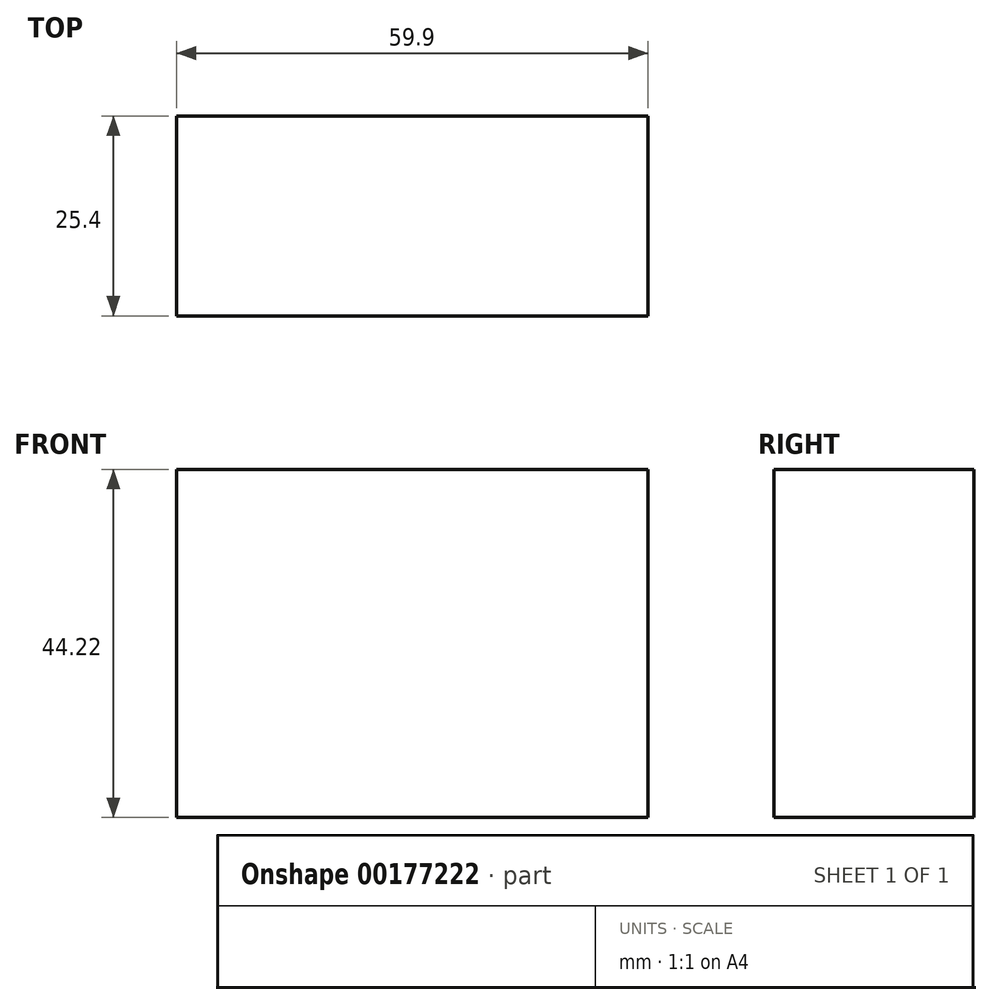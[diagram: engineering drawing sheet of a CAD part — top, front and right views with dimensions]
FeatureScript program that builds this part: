
annotation { "Feature Type Name" : "Feature", "Feature Type Description" : "" }
export const myFeature = defineFeature(function(context is Context, id is Id, definition is map)
    precondition{}
    {
        {
            var Q0;
            Q0=qCreatedBy(makeId("Front.planeOp"),FACE);
            var sketch = newSketch(context, id + "F0", { "sketchPlane" : qUnion([Q0])});
            skLineSegment(sketch, "E0.bottom", {"start": v(-42.5, 40.08) * mm, "end": v(17.4, 40.08) * mm});
            skLineSegment(sketch, "E0.top", {"start": v(-42.5, -4.14) * mm, "end": v(17.4, -4.14) * mm});
            skLineSegment(sketch, "E0.left", {"start": v(-42.5, 40.08) * mm, "end": v(-42.5, -4.14) * mm});
            skLineSegment(sketch, "E0.right", {"start": v(17.4, 40.08) * mm, "end": v(17.4, -4.14) * mm});
            skSolve(sketch);
        }
        {
            var Q0;
            Q0=makeQuery(id+"F0.imprint","IMPRINT",FACE,{"disambiguationData":[TD([[makeQuery(id+"F0.imprint","IMPRINT",EDGE,{"derivedFrom":sQuery(id+"F0.wireOp",EDGE,"E0.bottom")}),-1.0]])]});
            extrude(context, id + "F1", {"entities" : qUnion([Q0]), "depth" : 25.4 * mm});
        }
    });
